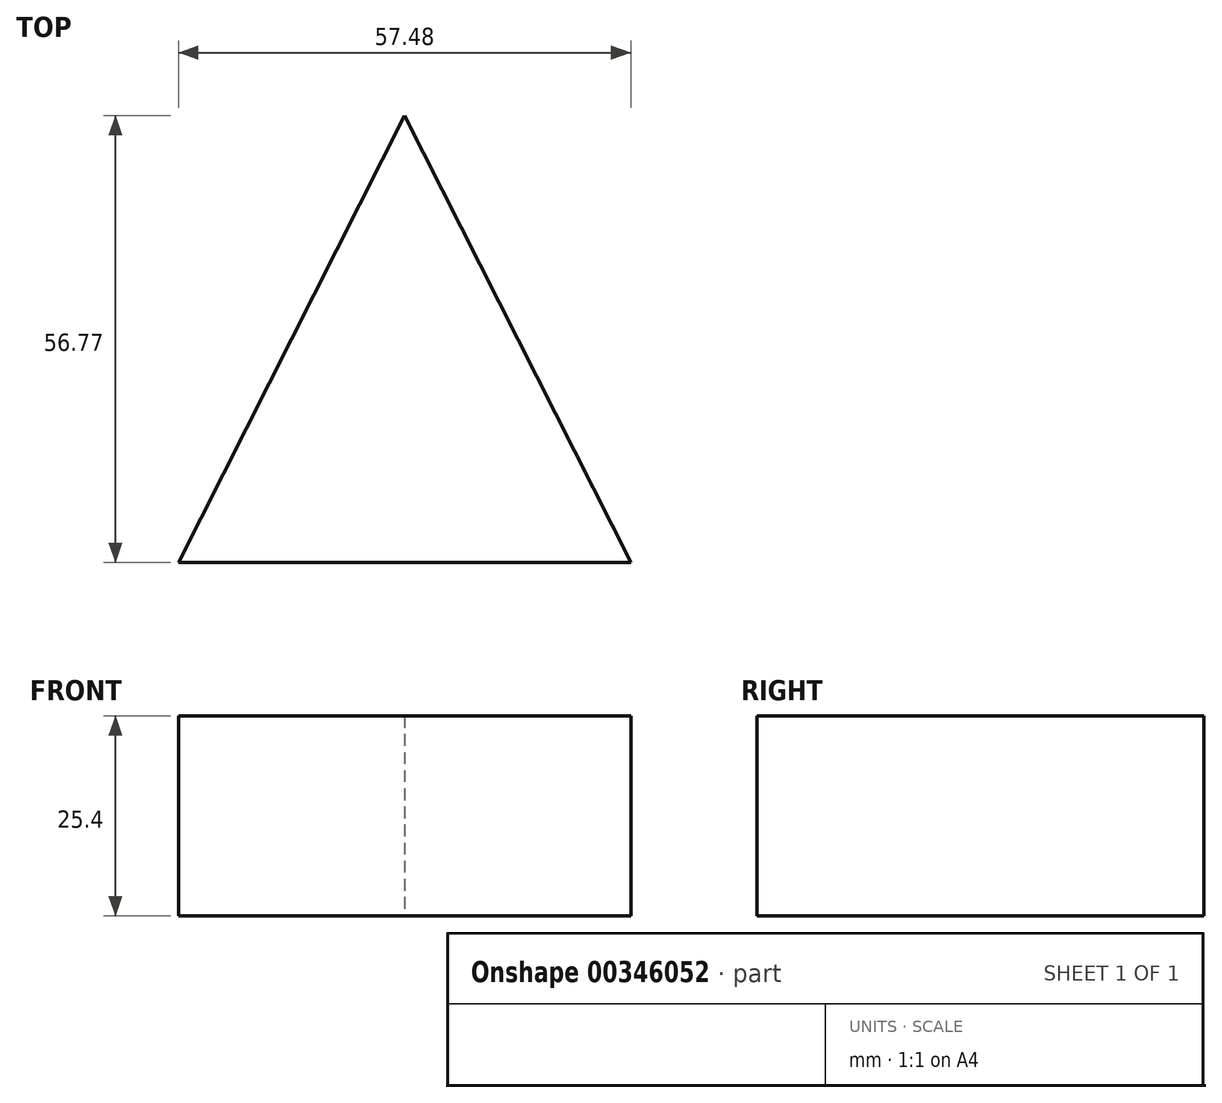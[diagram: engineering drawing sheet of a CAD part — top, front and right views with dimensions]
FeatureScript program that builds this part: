
annotation { "Feature Type Name" : "Feature", "Feature Type Description" : "" }
export const myFeature = defineFeature(function(context is Context, id is Id, definition is map)
    precondition{}
    {
        {
            var Q0;
            Q0=qCreatedBy(makeId("Top.planeOp"),FACE);
            var sketch = newSketch(context, id + "F0", { "sketchPlane" : qUnion([Q0])});
            skLineSegment(sketch, "E0", {"start": v(0, 56.77) * mm, "end": v(-28.74, 0) * mm});
            skLineSegment(sketch, "E1", {"start": v(-28.74, 0) * mm, "end": v(0, 56.77) * mm});
            skLineSegment(sketch, "E2", {"start": v(0, 56.77) * mm, "end": v(28.74, 0) * mm});
            skLineSegment(sketch, "E3", {"start": v(28.74, 0) * mm, "end": v(-28.74, 0) * mm});
            skArc(sketch, "E4", {"start": v(19.1, 19.03) * mm, "mid": v(0.4, 25.58) * mm, "end": v(-18.61, 20) * mm});
            skArc(sketch, "E5", {"start": v(-18.61, 20) * mm, "mid": v(-13.52, 6.09) * mm, "end": v(0, 0) * mm});
            skArc(sketch, "E6", {"start": v(0, 0) * mm, "mid": v(13.46, 5.59) * mm, "end": v(19.1, 19.03) * mm});
            skArc(sketch, "E7", {"start": v(0, 0) * mm, "mid": v(9.18, 12.8) * mm, "end": v(0, 25.59) * mm});
            skArc(sketch, "E8", {"start": v(0, 25.59) * mm, "mid": v(-9.18, 12.8) * mm, "end": v(0, 0) * mm});
            skSolve(sketch);
        }
        {
            var Q0;
            Q0 = qSketchRegion(id + "F0", true);
            extrude(context, id + "F1", {"entities" : qUnion([Q0]), "depth" : 25.4 * mm});
        }
    });
